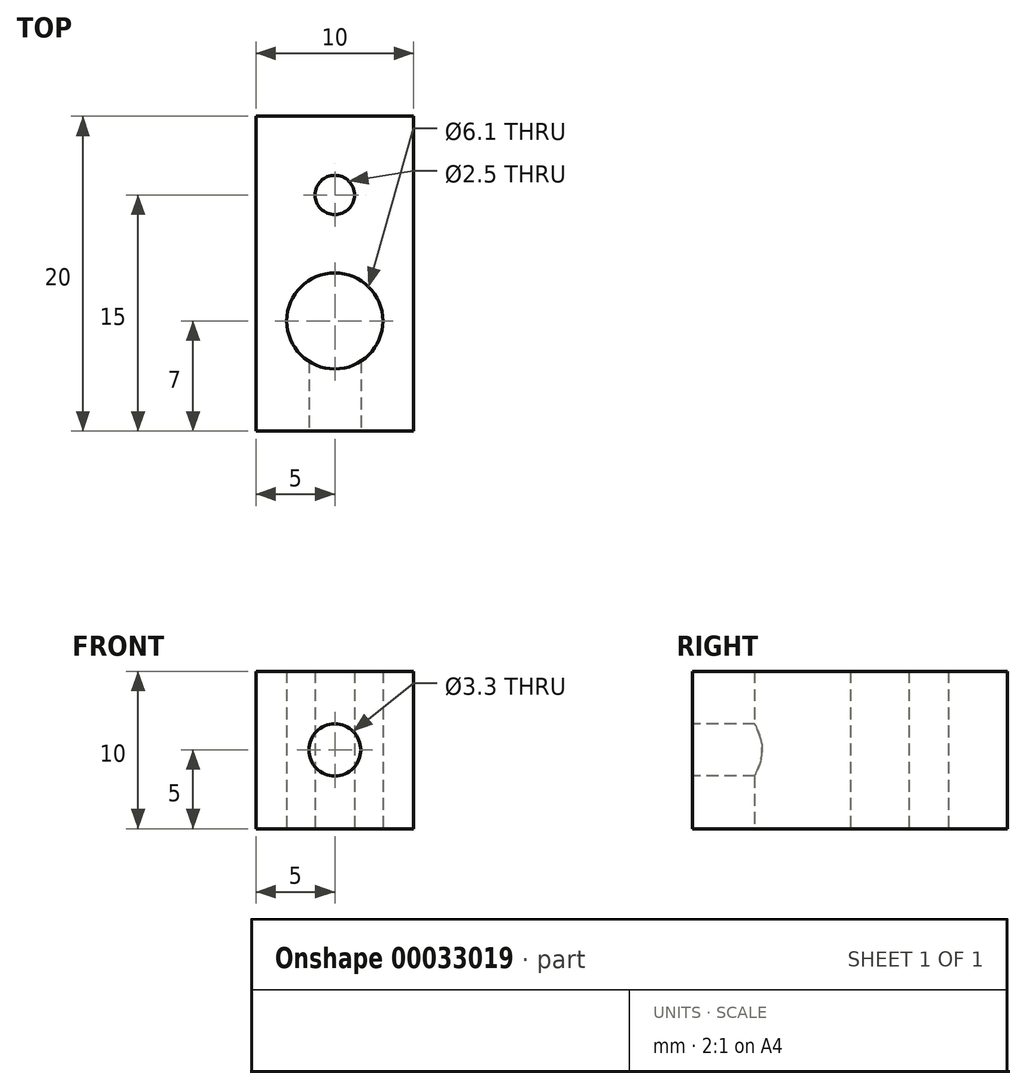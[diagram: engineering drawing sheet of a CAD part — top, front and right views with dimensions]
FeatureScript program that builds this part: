
annotation { "Feature Type Name" : "Feature", "Feature Type Description" : "" }
export const myFeature = defineFeature(function(context is Context, id is Id, definition is map)
    precondition{}
    {
        {
            var Q0;
            Q0=qCreatedBy(makeId("Top.planeOp"),FACE);
            var sketch = newSketch(context, id + "F0", { "sketchPlane" : qUnion([Q0])});
            skLineSegment(sketch, "E0.bottom", {"start": v(-5, 13) * mm, "end": v(5, 13) * mm});
            skLineSegment(sketch, "E0.top", {"start": v(-5, -7) * mm, "end": v(5, -7) * mm});
            skLineSegment(sketch, "E0.left", {"start": v(-5, 13) * mm, "end": v(-5, -7) * mm});
            skLineSegment(sketch, "E0.right", {"start": v(5, 13) * mm, "end": v(5, -7) * mm});
            skCircle(sketch, "E1", {"center": v(0, 0) * mm, "radius": 3.05 * mm});
            skCircle(sketch, "E2", {"center": v(0, 8) * mm, "radius": 1.25 * mm});
            skSolve(sketch);
        }
        {
            var Q0;
            Q0 = qSketchRegion(id + "F0", true);
            var Q1;
            Q1=makeQuery(id+"F0.imprint","IMPRINT",FACE,{"disambiguationData":[TD([[makeQuery(id+"F0.imprint","IMPRINT",EDGE,{"derivedFrom":sQuery(id+"F0.wireOp",EDGE,"E0.bottom")}),-1.0]])]});
            extrude(context, id + "F1", {"entities" : qUnion([Q0, Q1]), "depth" : 10 * mm});
        }
        {
            var Q0;
            Q0=makeQuery(id+"F1.opExtrude","SWEPT_FACE",FACE,{"disambiguationData":[OSD([sQuery(id+"F0.wireOp",EDGE,"E0.top")])]});
            var sketch = newSketch(context, id + "F2", { "sketchPlane" : qUnion([Q0])});
            skPoint(sketch, "E3", {"position": v(0, 5) * mm});
            skSolve(sketch);
        }
        {
            var Q0;
            Q0=sQuery(id+"F2.wireOp",VERTEX,"E3");
            var Q1;
            Q1=makeQuery(id+"F1.opExtrude","SWEPT_BODY",BODY,{"disambiguationData":[OSD([sQuery(id+"F0.wireOp",EDGE,"E0.bottom"),sQuery(id+"F0.wireOp",EDGE,"E0.top"),sQuery(id+"F0.wireOp",EDGE,"E0.left"),sQuery(id+"F0.wireOp",EDGE,"E0.right"),sQuery(id+"F0.wireOp",EDGE,"E1"),sQuery(id+"F0.wireOp",EDGE,"E2")])]});
            hole(context, id + "F3", {"style" : HoleStyle.SIMPLE, "holeDiameter" : 3.3 * mm, "endStyle" : HoleEndStyle.BLIND, "holeDepth" : 7 * mm, "locations" : qUnion([Q0]), "scope" : qUnion([Q1])});
        }
    });
